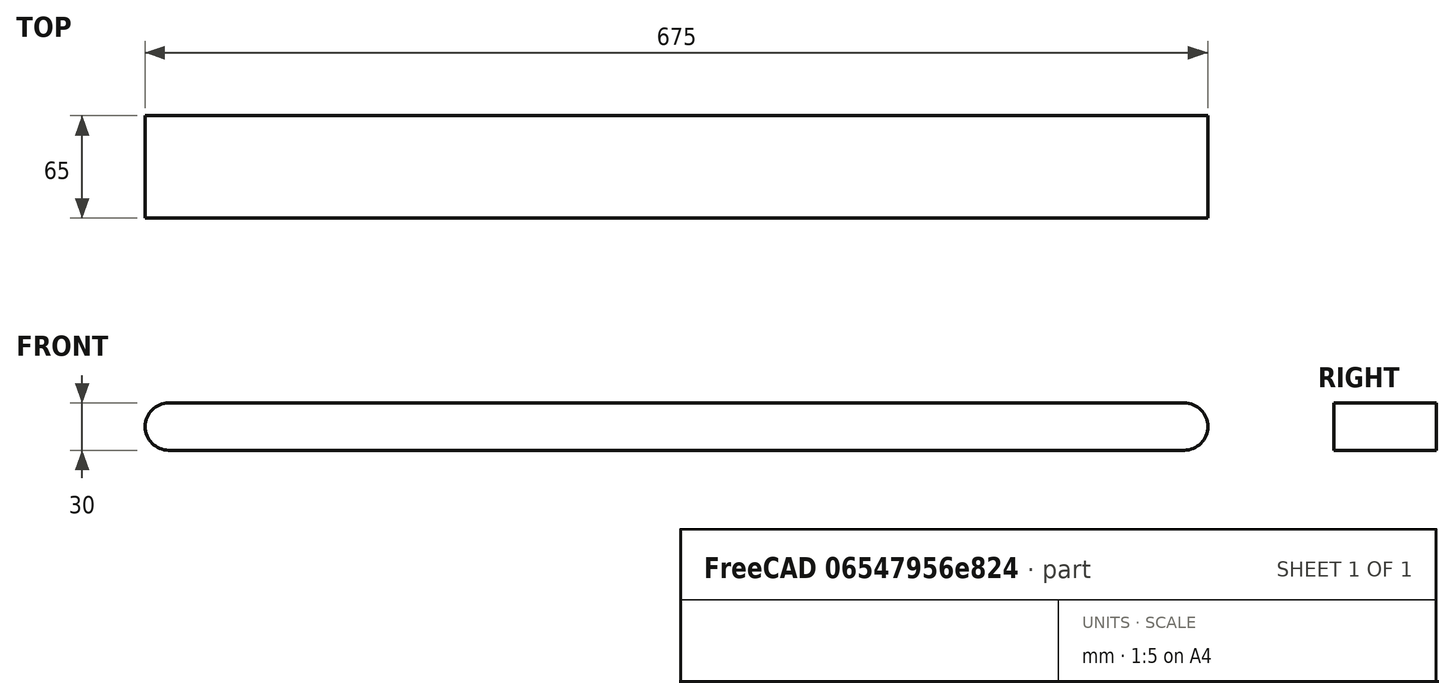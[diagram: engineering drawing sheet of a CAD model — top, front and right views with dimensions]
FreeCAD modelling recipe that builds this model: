
FCSTD DOCUMENT  (FreeCAD 1.0R39109 (Git))
Label: conveyor
License: All rights reserved
LicenseURL: https://en.wikipedia.org/wiki/All_rights_reserved
objects: Sketcher::SketchObject×1, PartDesign::Pad×1, PartDesign::Body×1
note: 6 computed .brp shape members not serialized (recipe doc carries the construction recipe); baked Part::Feature solids carry a one-line shape summary decoded from their .brp

FEATURE [Sketcher::SketchObject] Sketch
  ArcFitTolerance = 1e-06
  AttachmentSupport = -> [XZ_Plane]
  FullyConstrained = false
  MakeInternals = false
  MapMode = 5
  Placement = pos=(0,0,0) rot=(1,0,0;1.5708rad)
  sketch-geometry (4):
    g0: ArcOfCircle CenterX=723.279 CenterY=-81.4533 CenterZ=0 NormalX=0 NormalY=0 NormalZ=1 AngleXU=0 Radius=15 StartAngle=4.71239 EndAngle=7.85398
    g1: ArcOfCircle CenterX=78.2788 CenterY=-81.4533 CenterZ=0 NormalX=0 NormalY=0 NormalZ=1 AngleXU=0 Radius=15 StartAngle=1.5708 EndAngle=4.71239
    g2: LineSegment StartX=78.2788 StartY=-66.4533 StartZ=0 EndX=723.279 EndY=-66.4533 EndZ=0
    g3: LineSegment StartX=723.279 StartY=-96.4533 StartZ=0 EndX=78.2788 EndY=-96.4533 EndZ=0
  constraints (10):
    c: Radius(g0) = 15
    c: Angle(g0) = 3.14159
    c: Radius(g1) = 15
    c: Angle(g1) = 3.14159
    c: Coincident(g2,g1)
    c: Coincident(g2,g0)
    c: Horizontal(g2)
    c: Coincident(g3,g0)
    c: Coincident(g3,g1)
    c: Horizontal(g3)
FEATURE [PartDesign::Pad] Pad
  Direction = (0,-1,2e-16)
  Length = 65
  Length2 = 10
  Placement = pos=(0,0,0) rot=(1,0,0;1.5708rad)
  Profile = -> Sketch
  ReferenceAxis = -> Sketch [N_Axis]
  Refine = true
  Suppressed = false
  Type = 0
FEATURE [PartDesign::Body] Body
  AllowCompound = false
  Group = -> [Sketch,Pad]
  Origin = -> Origin
  Tip = -> Pad
